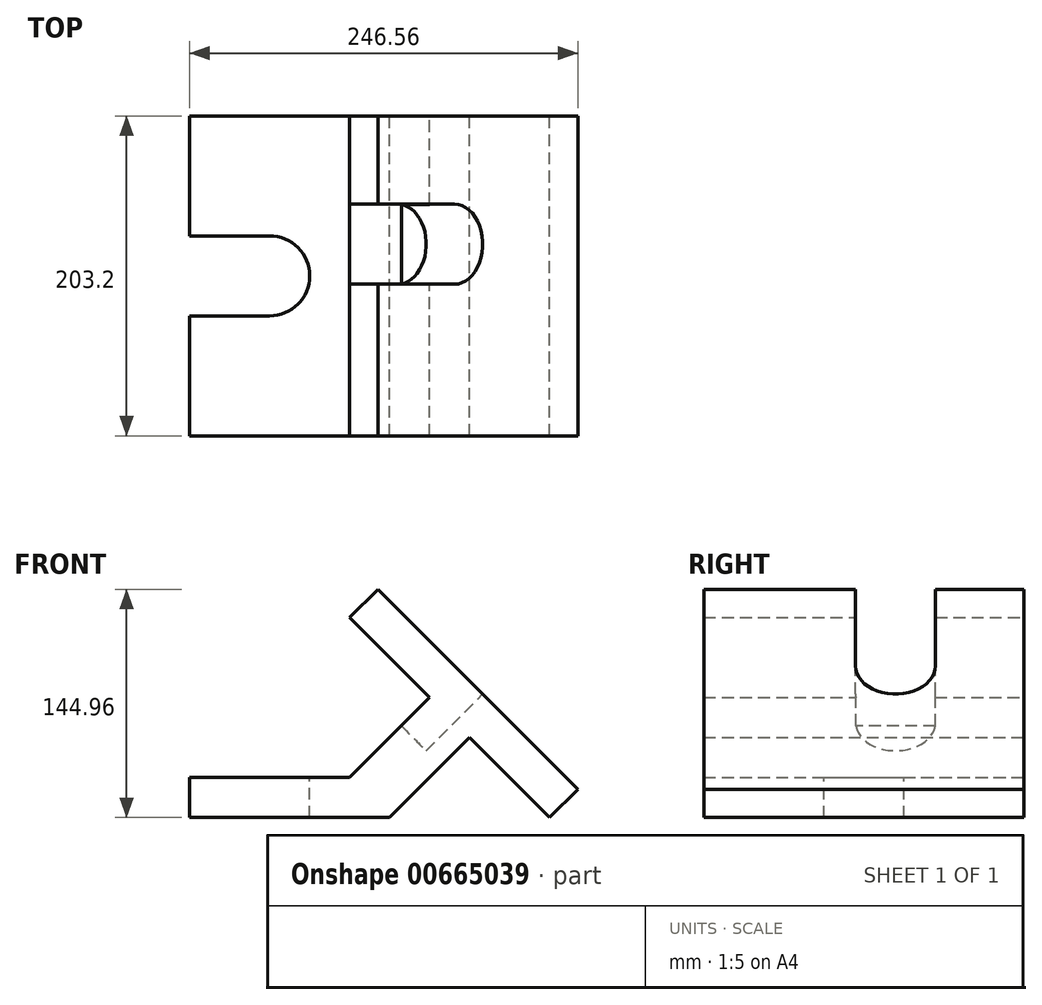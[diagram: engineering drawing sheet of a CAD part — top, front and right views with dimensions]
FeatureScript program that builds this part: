
annotation { "Feature Type Name" : "Feature", "Feature Type Description" : "" }
export const myFeature = defineFeature(function(context is Context, id is Id, definition is map)
    precondition{}
    {
        {
            var Q0;
            Q0=qCreatedBy(makeId("Front.planeOp"),FACE);
            var sketch = newSketch(context, id + "F0", { "sketchPlane" : qUnion([Q0])});
            skLineSegment(sketch, "E0", {"start": v(0, 0) * mm, "end": v(127, 0) * mm});
            skLineSegment(sketch, "E1", {"start": v(177.8, 50.8) * mm, "end": v(127, 0) * mm});
            skLineSegment(sketch, "E2", {"start": v(0, 0) * mm, "end": v(0, 25.4) * mm});
            skLineSegment(sketch, "E3", {"start": v(0, 25.4) * mm, "end": v(101.6, 25.4) * mm});
            skLineSegment(sketch, "E4", {"start": v(152.4, 76.2) * mm, "end": v(101.6, 25.4) * mm});
            skLineSegment(sketch, "E5", {"start": v(228.6, 0) * mm, "end": v(177.8, 50.8) * mm});
            skLineSegment(sketch, "E6", {"start": v(101.6, 127) * mm, "end": v(152.4, 76.2) * mm});
            skLineSegment(sketch, "E7", {"start": v(246.56, 17.96) * mm, "end": v(228.6, 0) * mm});
            skLineSegment(sketch, "E8", {"start": v(119.56, 144.96) * mm, "end": v(101.6, 127) * mm});
            skLineSegment(sketch, "E9", {"start": v(246.56, 17.96) * mm, "end": v(119.56, 144.96) * mm});
            skSolve(sketch);
        }
        {
            var Q0;
            Q0=makeQuery(id+"F0.imprint","IMPRINT",FACE,{"disambiguationData":[TD([[makeQuery(id+"F0.imprint","IMPRINT",EDGE,{"derivedFrom":sQuery(id+"F0.wireOp",EDGE,"E0")}),1.0]])]});
            extrude(context, id + "F1", {"entities" : qUnion([Q0]), "endBound" : BoundingType.SYMMETRIC, "depth" : 203.2 * mm, "offsetDistance" : 25.4 * mm});
        }
        {
            var Q0;
            Q0=makeQuery(id+"F1.opExtrude","SWEPT_FACE",FACE,{"disambiguationData":[OSD([sQuery(id+"F0.wireOp",EDGE,"E9")])]});
            var sketch = newSketch(context, id + "F2", { "sketchPlane" : qUnion([Q0])});
            skLineSegment(sketch, "E10.0", {"start": v(-5.26, -50.8) * mm, "end": v(-5.26, 50.8) * mm});
            skLineSegment(sketch, "E11.0", {"start": v(148.94, -50.8) * mm, "end": v(148.94, 50.8) * mm});
            skLineSegment(sketch, "E12.0", {"start": v(98.14, -50.8) * mm, "end": v(98.14, 50.8) * mm});
            skLineSegment(sketch, "E13.0", {"start": v(45.54, -50.8) * mm, "end": v(45.54, 50.8) * mm});
            skLineSegment(sketch, "E14.0", {"start": v(123.54, 76.2) * mm, "end": v(123.54, 76.2) * mm});
            skLineSegment(sketch, "E15.0", {"start": v(123.54, -76.2) * mm, "end": v(123.54, -76.2) * mm});
            skLineSegment(sketch, "E16.trimOffspring", {"start": v(20.14, -76.2) * mm, "end": v(20.14, -76.2) * mm});
            skLineSegment(sketch, "E17.trimOffspring", {"start": v(20.14, 76.2) * mm, "end": v(20.14, 76.2) * mm});
            skPoint(sketch, "E18.visualSharp", {"position": v(-5.26, -76.2) * mm});
            skArc(sketch, "E18.filletArc", {"start": v(-5.26, -50.8) * mm, "mid": v(2.18, -68.76) * mm, "end": v(20.14, -76.2) * mm});
            skPoint(sketch, "E19.visualSharp", {"position": v(45.54, -76.2) * mm});
            skArc(sketch, "E19.filletArc", {"start": v(20.14, -76.2) * mm, "mid": v(38.1, -68.76) * mm, "end": v(45.54, -50.8) * mm});
            skPoint(sketch, "E20.visualSharp", {"position": v(45.54, 76.2) * mm});
            skArc(sketch, "E20.filletArc", {"start": v(45.54, 50.8) * mm, "mid": v(38.1, 68.76) * mm, "end": v(20.14, 76.2) * mm});
            skPoint(sketch, "E21.visualSharp", {"position": v(-5.26, 76.2) * mm});
            skArc(sketch, "E21.filletArc", {"start": v(20.14, 76.2) * mm, "mid": v(2.18, 68.76) * mm, "end": v(-5.26, 50.8) * mm});
            skPoint(sketch, "E22.visualSharp", {"position": v(98.14, 76.2) * mm});
            skArc(sketch, "E22.filletArc", {"start": v(123.54, 76.2) * mm, "mid": v(105.58, 68.76) * mm, "end": v(98.14, 50.8) * mm});
            skPoint(sketch, "E23.visualSharp", {"position": v(148.94, 76.2) * mm});
            skArc(sketch, "E23.filletArc", {"start": v(148.94, 50.8) * mm, "mid": v(141.5, 68.76) * mm, "end": v(123.54, 76.2) * mm});
            skPoint(sketch, "E24.visualSharp", {"position": v(148.94, -76.2) * mm});
            skArc(sketch, "E24.filletArc", {"start": v(123.54, -76.2) * mm, "mid": v(141.5, -68.76) * mm, "end": v(148.94, -50.8) * mm});
            skPoint(sketch, "E25.visualSharp", {"position": v(98.14, -76.2) * mm});
            skArc(sketch, "E25.filletArc", {"start": v(98.14, -50.8) * mm, "mid": v(105.58, -68.76) * mm, "end": v(123.54, -76.2) * mm});
            skSolve(sketch);
        }
        {
            var Q0;
            Q0=makeQuery(id+"F2.imprint","IMPRINT",FACE,{"disambiguationData":[TD([[makeQuery(id+"F2.imprint","IMPRINT",EDGE,{"derivedFrom":sQuery(id+"F2.wireOp",EDGE,"E11.0")}),1.0]])]});
            var Q1;
            Q1=makeQuery(id+"F2.imprint","IMPRINT",FACE,{"disambiguationData":[TD([[makeQuery(id+"F2.imprint","IMPRINT",EDGE,{"derivedFrom":sQuery(id+"F2.wireOp",EDGE,"E10.0")}),-1.0]])]});
            extrude(context, id + "F3", {"entities" : qUnion([Q0, Q1]), "operationType" : NewBodyOperationType.REMOVE, "oppositeDirection" : true, "depth" : 50.8 * mm, "offsetDistance" : 25.4 * mm});
        }
        {
            var Q0;
            Q0=makeQuery(id+"F1.opExtrude","SWEPT_FACE",FACE,{"disambiguationData":[OSD([sQuery(id+"F0.wireOp",EDGE,"E3")])]});
            var sketch = newSketch(context, id + "F4", { "sketchPlane" : qUnion([Q0])});
            skLineSegment(sketch, "E26", {"start": v(50.8, -25.4) * mm, "end": v(0, -25.4) * mm});
            skLineSegment(sketch, "E27", {"start": v(50.8, 25.4) * mm, "end": v(0, 25.4) * mm});
            skArc(sketch, "E28", {"start": v(50.8, -25.4) * mm, "mid": v(76.2, 0) * mm, "end": v(50.8, 25.4) * mm});
            skSolve(sketch);
        }
        {
            var Q0;
            {var subQ0=sQuery(id+"F4.wireOp",EDGE,"E26");Q0=makeQuery(id+"F4.imprint","IMPRINT",FACE,{"disambiguationData":[TD([[makeQuery(id+"F4.imprint","IMPRINT",EDGE,{"derivedFrom":subQ0}),-1.0]])]});}
            extrude(context, id + "F5", {"entities" : qUnion([Q0]), "operationType" : NewBodyOperationType.REMOVE, "oppositeDirection" : true, "depth" : 38.1 * mm, "offsetDistance" : 25.4 * mm});
        }
    });
